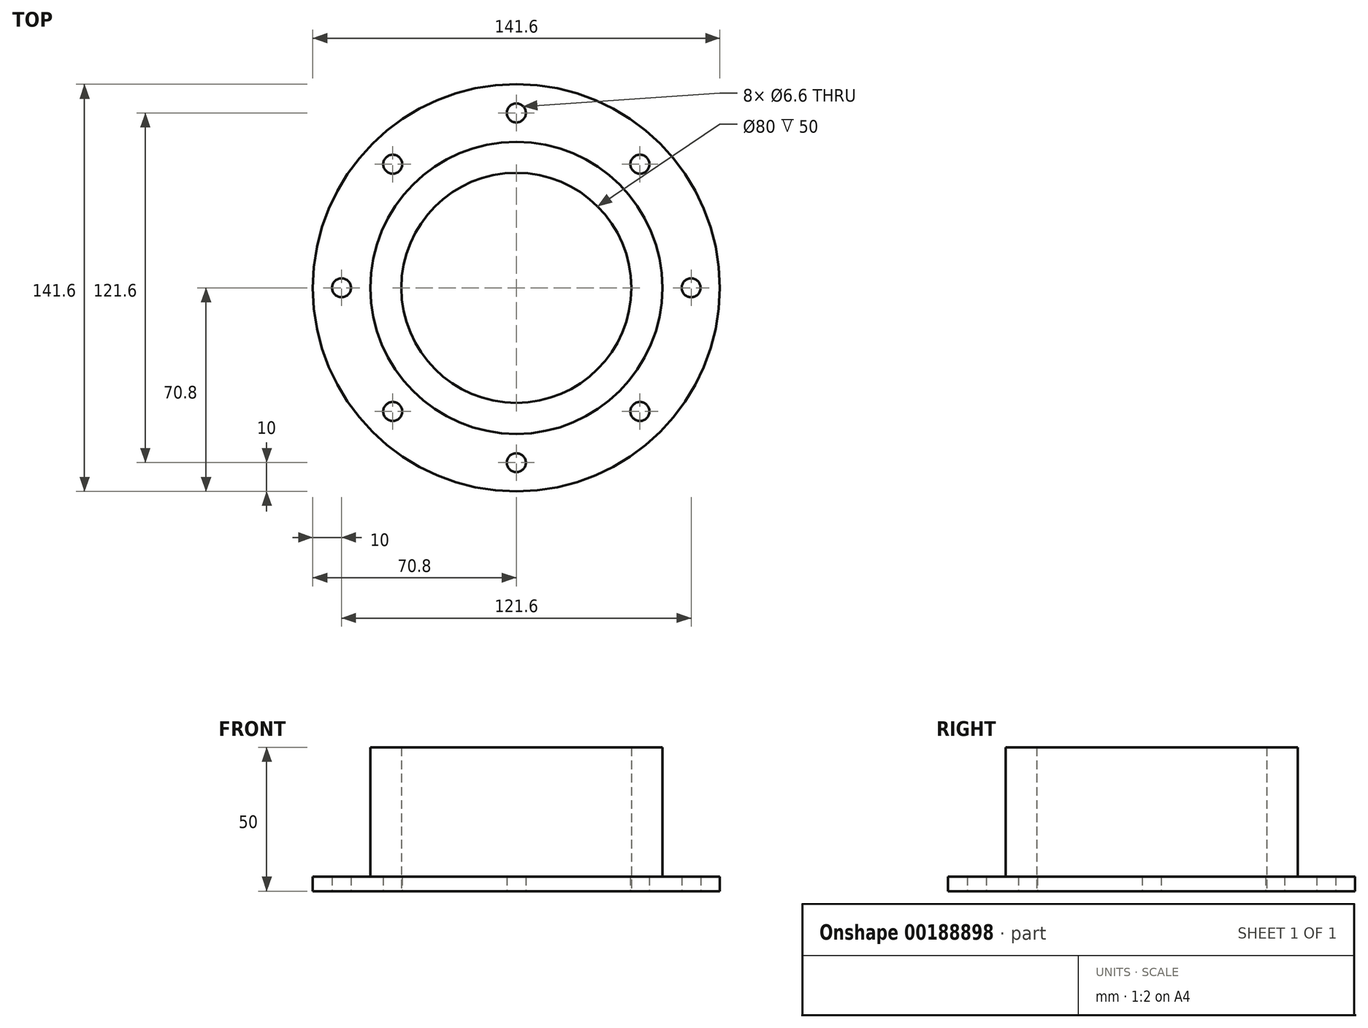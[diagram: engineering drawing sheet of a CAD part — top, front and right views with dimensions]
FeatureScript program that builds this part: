
annotation { "Feature Type Name" : "Feature", "Feature Type Description" : "" }
export const myFeature = defineFeature(function(context is Context, id is Id, definition is map)
    precondition{}
    {
        {
            var Q0;
            Q0=qCreatedBy(makeId("Top.planeOp"),FACE);
            var sketch = newSketch(context, id + "F0", { "sketchPlane" : qUnion([Q0])});
            skCircle(sketch, "E0", {"center": v(0, 0) * mm, "radius": 50.8 * mm});
            skCircle(sketch, "E1", {"center": v(0, 0) * mm, "radius": 40 * mm});
            skSolve(sketch);
        }
        {
            var Q0;
            Q0=makeQuery(id+"F0.imprint","IMPRINT",FACE,{"disambiguationData":[TD([[makeQuery(id+"F0.imprint","IMPRINT",EDGE,{"derivedFrom":sQuery(id+"F0.wireOp",EDGE,"E0")}),1.0]])]});
            extrude(context, id + "F1", {"entities" : qUnion([Q0]), "depth" : 50 * mm});
        }
        {
            var Q0;
            Q0=qCreatedBy(makeId("Top.planeOp"),FACE);
            var sketch = newSketch(context, id + "F2", { "sketchPlane" : qUnion([Q0])});
            skCircle(sketch, "E2", {"center": v(0, 0) * mm, "radius": 70.8 * mm});
            skCircle(sketch, "E3", {"center": v(0, 0) * mm, "radius": 50.8 * mm});
            skCircle(sketch, "E4", {"center": v(0, 60.8) * mm, "radius": 3.3 * mm});
            skCircle(sketch, "E5.1.0", {"center": v(43, 43) * mm, "radius": 3.3 * mm});
            skCircle(sketch, "E5.2.0", {"center": v(60.8, 0) * mm, "radius": 3.3 * mm});
            skCircle(sketch, "E5.3.0", {"center": v(43, -43) * mm, "radius": 3.3 * mm});
            skCircle(sketch, "E5.4.0", {"center": v(0, -60.8) * mm, "radius": 3.3 * mm});
            skCircle(sketch, "E5.5.0", {"center": v(-43, -43) * mm, "radius": 3.3 * mm});
            skCircle(sketch, "E5.6.0", {"center": v(-60.8, 0) * mm, "radius": 3.3 * mm});
            skCircle(sketch, "E5.7.0", {"center": v(-43, 43) * mm, "radius": 3.3 * mm});
            skLineSegment(sketch, "E5.anchor1", {"start": v(0, 0) * mm, "end": v(0, 60.8) * mm, "construction": true});
            skLineSegment(sketch, "E5.anchor2", {"start": v(0, 0) * mm, "end": v(0, 60.8) * mm, "construction": true});
            skSolve(sketch);
        }
        {
            var Q0;
            Q0=makeQuery(id+"F2.imprint","IMPRINT",FACE,{"disambiguationData":[TD([[makeQuery(id+"F2.imprint","IMPRINT",EDGE,{"derivedFrom":sQuery(id+"F2.wireOp",EDGE,"E2")}),1.0]])]});
            extrude(context, id + "F3", {"entities" : qUnion([Q0]), "operationType" : NewBodyOperationType.ADD, "depth" : 5 * mm});
        }
    });
